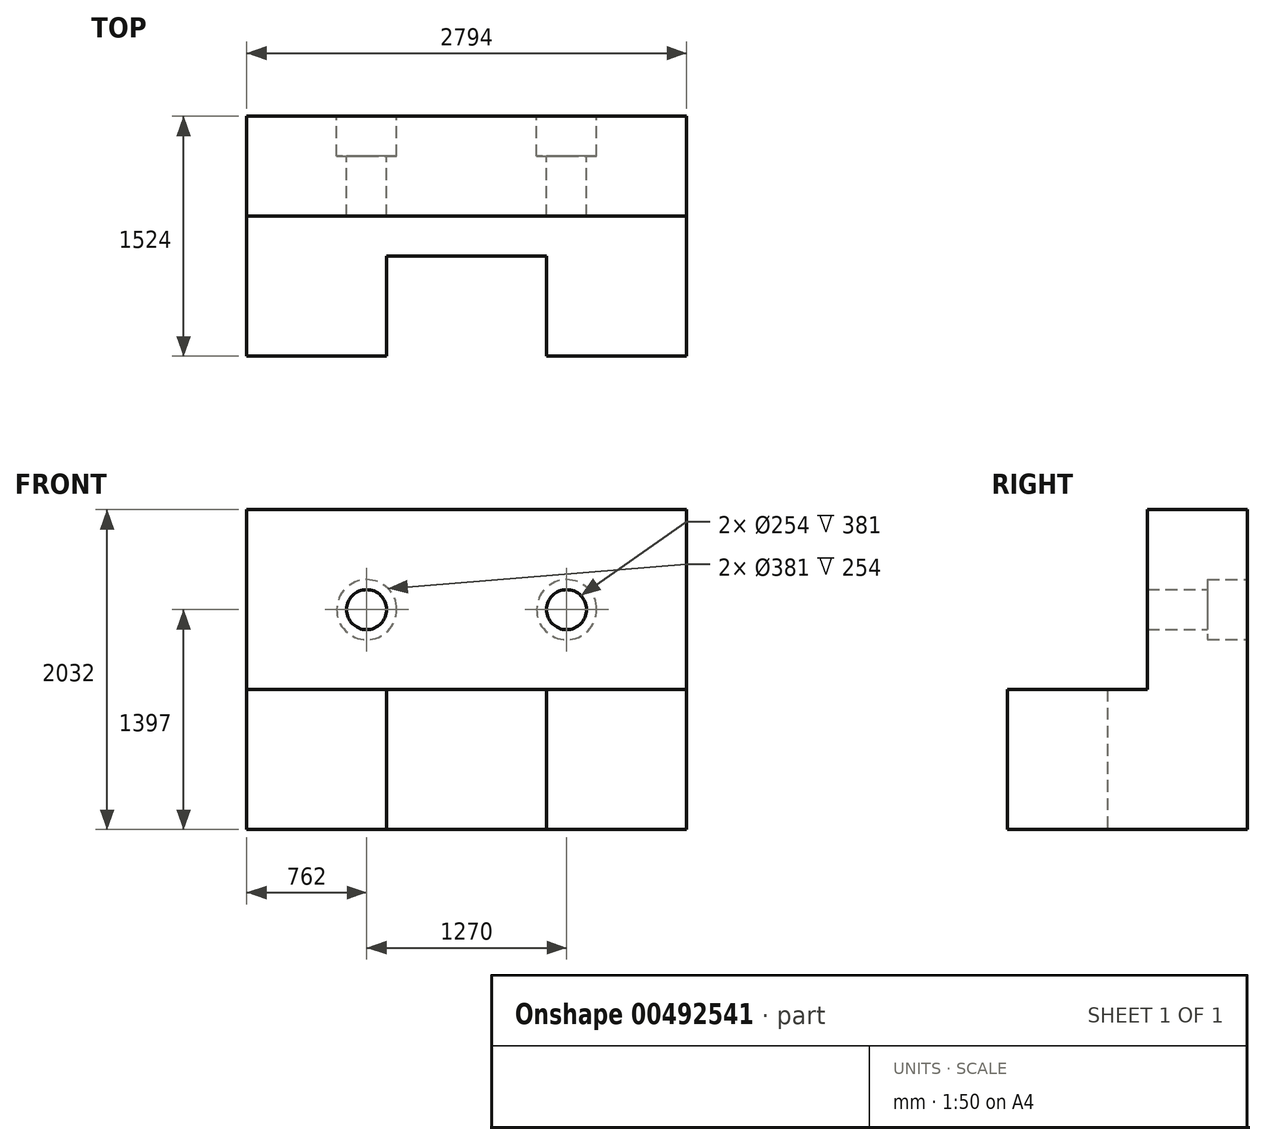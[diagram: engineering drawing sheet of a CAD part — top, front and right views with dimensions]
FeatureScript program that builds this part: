
annotation { "Feature Type Name" : "Feature", "Feature Type Description" : "" }
export const myFeature = defineFeature(function(context is Context, id is Id, definition is map)
    precondition{}
    {
        {
            var Q0;
            Q0=qCreatedBy(makeId("Front.planeOp"),FACE);
            var sketch = newSketch(context, id + "F0", { "sketchPlane" : qUnion([Q0])});
            skLineSegment(sketch, "E0.bottom", {"start": v(0, 0) * mm, "end": v(2794, 0) * mm});
            skLineSegment(sketch, "E0.top", {"start": v(0, 2032) * mm, "end": v(2794, 2032) * mm});
            skLineSegment(sketch, "E0.left", {"start": v(0, 0) * mm, "end": v(0, 2032) * mm});
            skLineSegment(sketch, "E0.right", {"start": v(2794, 0) * mm, "end": v(2794, 2032) * mm});
            skCircle(sketch, "E1", {"center": v(762, 1397) * mm, "radius": 127 * mm});
            skCircle(sketch, "E2", {"center": v(2032, 1397) * mm, "radius": 127 * mm});
            skSolve(sketch);
        }
        {
            var Q0;
            Q0 = qSketchRegion(id + "F0", true);
            var Q1;
            Q1=makeQuery(id+"F0.imprint","IMPRINT",FACE,{"disambiguationData":[TD([[makeQuery(id+"F0.imprint","IMPRINT",EDGE,{"derivedFrom":sQuery(id+"F0.wireOp",EDGE,"E1")}),1.0]])]});
            var Q2;
            Q2=makeQuery(id+"F0.imprint","IMPRINT",FACE,{"disambiguationData":[TD([[makeQuery(id+"F0.imprint","IMPRINT",EDGE,{"derivedFrom":sQuery(id+"F0.wireOp",EDGE,"E2")}),1.0]])]});
            extrude(context, id + "F1", {"entities" : qUnion([Q0, Q1, Q2]), "offsetDistance" : 25.4 * mm, "depth" : 635 * mm});
        }
        {
            var Q0;
            Q0=sQuery(id+"F0.wireOp",VERTEX,"E2.center");
            var Q1;
            Q1=sQuery(id+"F0.wireOp",VERTEX,"E1.center");
            var Q2;
            Q2=makeQuery(id+"F1.opExtrude","SWEPT_BODY",BODY,{"disambiguationData":[OSD([sQuery(id+"F0.wireOp",EDGE,"E0.bottom"),sQuery(id+"F0.wireOp",EDGE,"E0.top"),sQuery(id+"F0.wireOp",EDGE,"E0.left"),sQuery(id+"F0.wireOp",EDGE,"E0.right")])]});
            hole(context, id + "F2", {"style" : HoleStyle.C_BORE, "endStyle" : HoleEndStyle.THROUGH, "oppositeDirection" : true, "holeDiameter" : 254 * mm, "cBoreDiameter" : 381 * mm, "cBoreDepth" : 254 * mm, "majorDiameter" : 6.35 * mm, "isTappedThrough" : true, "tappedDepth" : 12.7 * mm, "tapClearance" : 3, "startFromSketch" : true, "locations" : qUnion([Q0, Q1]), "scope" : qUnion([Q2])});
        }
        {
            var Q0;
            Q0=makeQuery(id+"F1.opExtrude","SWEPT_FACE",FACE,{"disambiguationData":[OSD([sQuery(id+"F0.wireOp",EDGE,"E0.bottom")])]});
            var sketch = newSketch(context, id + "F3", { "sketchPlane" : qUnion([Q0])});
            skLineSegment(sketch, "E3", {"start": v(0, 635) * mm, "end": v(0, 1524) * mm});
            skLineSegment(sketch, "E4", {"start": v(0, 1524) * mm, "end": v(889, 1524) * mm});
            skLineSegment(sketch, "E5", {"start": v(889, 1524) * mm, "end": v(889, 889) * mm});
            skLineSegment(sketch, "E6", {"start": v(889, 889) * mm, "end": v(1905, 889) * mm});
            skLineSegment(sketch, "E7", {"start": v(1905, 889) * mm, "end": v(1905, 1524) * mm});
            skLineSegment(sketch, "E8", {"start": v(1905, 1524) * mm, "end": v(2794, 1524) * mm});
            skLineSegment(sketch, "E9", {"start": v(2794, 1524) * mm, "end": v(2794, 635) * mm});
            skSolve(sketch);
        }
        {
            var Q0;
            Q0 = qSketchRegion(id + "F3", true);
            var Q1;
            Q1=makeQuery(id+"F3.imprint","IMPRINT",FACE,{"disambiguationData":[TD([[makeQuery(id+"F3.imprint","IMPRINT",EDGE,{"derivedFrom":sQuery(id+"F3.wireOp",EDGE,"E3")}),-1.0]])]});
            extrude(context, id + "F4", {"entities" : qUnion([Q0, Q1]), "operationType" : NewBodyOperationType.ADD, "oppositeDirection" : true, "depth" : 889 * mm});
        }
    });
